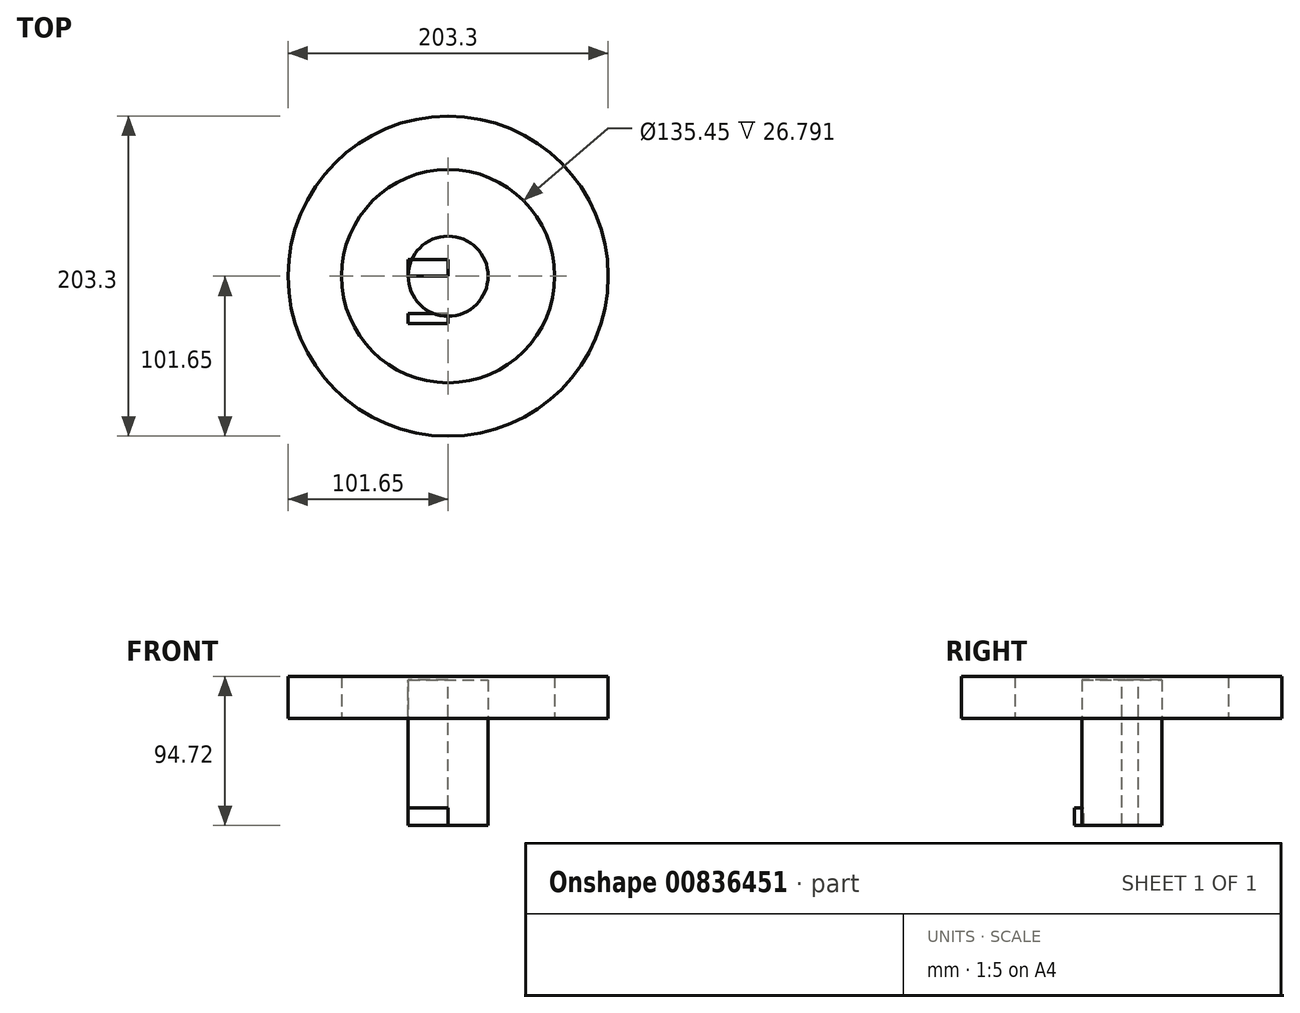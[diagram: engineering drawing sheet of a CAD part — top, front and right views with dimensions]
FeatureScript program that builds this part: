
annotation { "Feature Type Name" : "Feature", "Feature Type Description" : "" }
export const myFeature = defineFeature(function(context is Context, id is Id, definition is map)
    precondition{}
    {
        {
            var Q0;
            Q0=qCreatedBy(makeId("Right.planeOp"),FACE);
            var sketch = newSketch(context, id + "F0", { "sketchPlane" : qUnion([Q0])});
            skLineSegment(sketch, "E0.bottom", {"start": v(-29.98, 39.05) * mm, "end": v(-23.83, 39.05) * mm});
            skLineSegment(sketch, "E0.top", {"start": v(-29.98, 50.23) * mm, "end": v(-23.83, 50.23) * mm});
            skLineSegment(sketch, "E0.left", {"start": v(-29.98, 39.05) * mm, "end": v(-29.98, 50.23) * mm});
            skLineSegment(sketch, "E0.right", {"start": v(-23.83, 39.05) * mm, "end": v(-23.83, 50.23) * mm});
            skLineSegment(sketch, "E1.bottom", {"start": v(10.58, 39.05) * mm, "end": v(0, 39.05) * mm});
            skLineSegment(sketch, "E1.top", {"start": v(10.58, 131.6) * mm, "end": v(0, 131.6) * mm});
            skLineSegment(sketch, "E1.left", {"start": v(10.58, 39.05) * mm, "end": v(10.58, 131.6) * mm});
            skLineSegment(sketch, "E1.right", {"start": v(0, 39.05) * mm, "end": v(0, 131.6) * mm});
            skSolve(sketch);
        }
        {
            var Q0;
            Q0 = qSketchRegion(id + "F0", true);
            extrude(context, id + "F1", {"entities" : qUnion([Q0]), "depth" : 25.4 * mm, "offsetDistance" : 25.4 * mm});
        }
        {
            var Q0;
            Q0=qCreatedBy(makeId("Front.planeOp"),FACE);
            var sketch = newSketch(context, id + "F2", { "sketchPlane" : qUnion([Q0])});
            skCircle(sketch, "E2", {"center": v(-22.93, -60.3) * mm, "radius": 24.63 * mm});
            skSolve(sketch);
        }
        {
            var Q0;
            Q0=sQuery(id+"F2.wireOp",EDGE,"E2");
            var Q1;
            Q1=makeQuery(id+"F1.opExtrude","CAP_EDGE",EDGE,{"disambiguationData":[OSD([sQuery(id+"F0.wireOp",EDGE,"E1.left")])],"isStart":false});
            revolve(context, id + "F3", {"bodyType" : ToolBodyType.SURFACE, "surfaceOperationType" : NewSurfaceOperationType.NEW, "surfaceEntities" : qUnion([Q0]), "axis" : qUnion([Q1]), "revolveType" : RevolveType.FULL});
        }
        {
            var Q0;
            Q0=qCreatedBy(makeId("Front.planeOp"),FACE);
            var sketch = newSketch(context, id + "F4", { "sketchPlane" : qUnion([Q0])});
            skLineSegment(sketch, "E3.bottom", {"start": v(-42.32, 106.98) * mm, "end": v(-76.25, 106.98) * mm});
            skLineSegment(sketch, "E3.top", {"start": v(-42.32, 133.77) * mm, "end": v(-76.25, 133.77) * mm});
            skLineSegment(sketch, "E3.left", {"start": v(-42.32, 106.98) * mm, "end": v(-42.32, 133.77) * mm});
            skLineSegment(sketch, "E3.right", {"start": v(-76.25, 106.98) * mm, "end": v(-76.25, 133.77) * mm});
            skPoint(sketch, "E3.middle", {"position": v(-59.29, 120.37) * mm});
            skSolve(sketch);
        }
        {
            var Q0;
            Q0 = qSketchRegion(id + "F4", true);
            var Q1;
            Q1=makeQuery(id+"F1.opExtrude","SWEPT_FACE",FACE,{"disambiguationData":[OSD([sQuery(id+"F0.wireOp",EDGE,"E1.right")])]});
            var Q2;
            Q2=makeQuery(id+"F1.opExtrude","CAP_EDGE",EDGE,{"disambiguationData":[OSD([sQuery(id+"F0.wireOp",EDGE,"E1.right")])],"isStart":false});
            revolve(context, id + "F5", {"surfaceOperationType" : NewSurfaceOperationType.NEW, "entities" : qUnion([Q0, Q1]), "axis" : qUnion([Q2]), "revolveType" : RevolveType.FULL});
        }
        {
            var Q0;
            Q0=qCreatedBy(makeId("Right.planeOp"),FACE);
            var sketch = newSketch(context, id + "F6", { "sketchPlane" : qUnion([Q0])});
            skArc(sketch, "E4", {"start": v(-177.7, 121) * mm, "mid": v(-164.4, 63.37) * mm, "end": v(-201.05, 16.96) * mm});
            skSolve(sketch);
        }
        {
            var Q0;
            Q0=sQuery(id+"F6.wireOp",EDGE,"E4");
            var Q1;
            Q1=makeQuery(id+"F1.opExtrude","CAP_EDGE",EDGE,{"disambiguationData":[OSD([sQuery(id+"F0.wireOp",EDGE,"E0.left")])],"isStart":false});
            revolve(context, id + "F7", {"bodyType" : ToolBodyType.SURFACE, "surfaceOperationType" : NewSurfaceOperationType.NEW, "surfaceEntities" : qUnion([Q0]), "axis" : qUnion([Q1]), "revolveType" : RevolveType.FULL});
        }
    });
